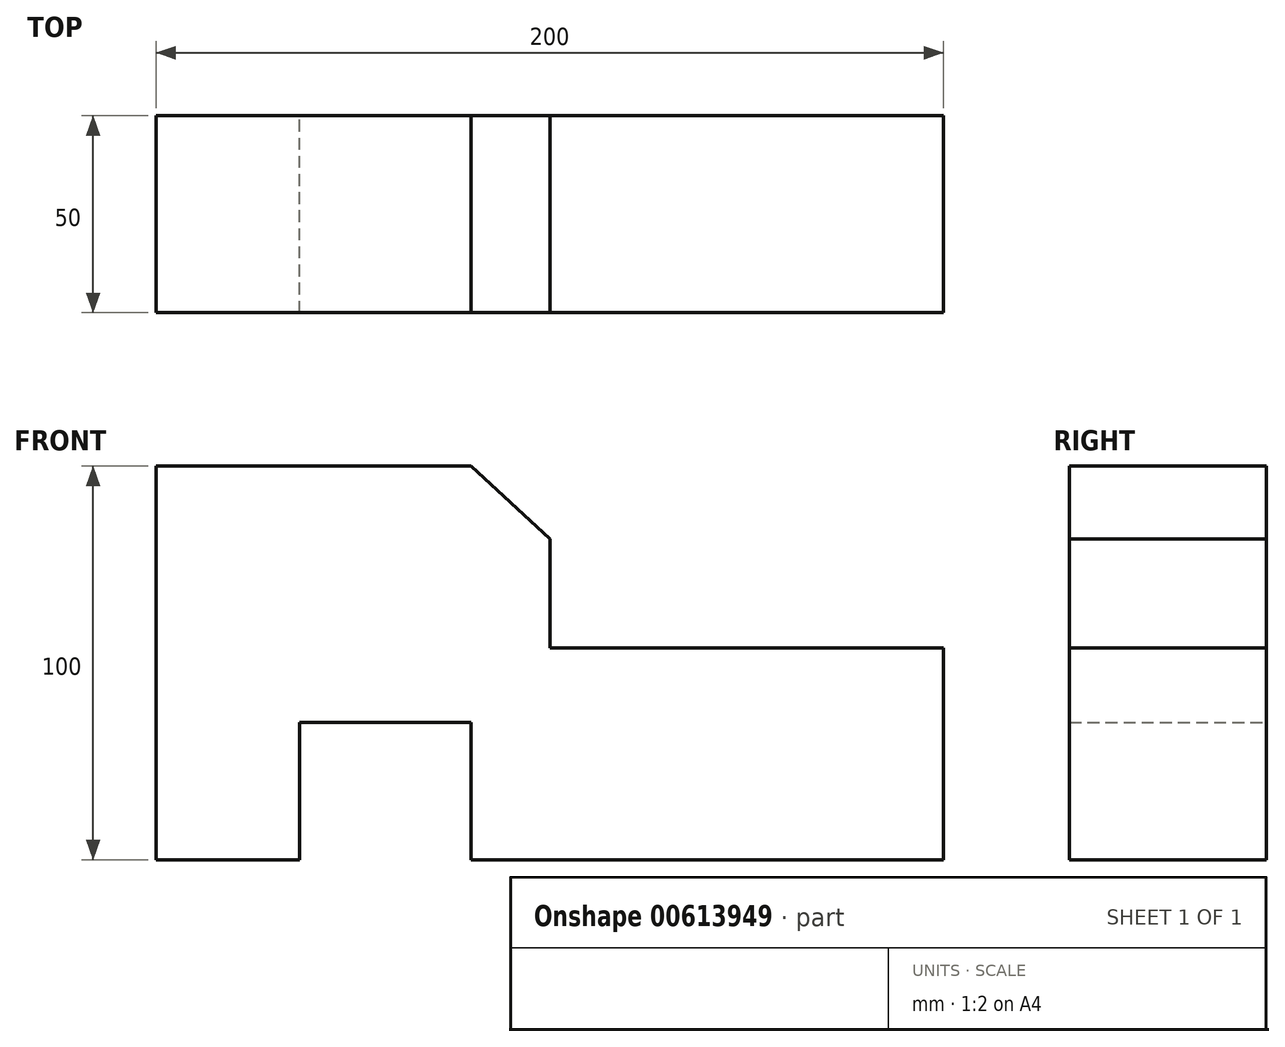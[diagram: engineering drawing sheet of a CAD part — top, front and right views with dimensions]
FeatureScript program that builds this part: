
annotation { "Feature Type Name" : "Feature", "Feature Type Description" : "" }
export const myFeature = defineFeature(function(context is Context, id is Id, definition is map)
    precondition{}
    {
        {
            var Q0;
            Q0=qCreatedBy(makeId("Front.planeOp"),FACE);
            var sketch = newSketch(context, id + "F0", { "sketchPlane" : qUnion([Q0])});
            skLineSegment(sketch, "E0", {"start": v(0, 0) * mm, "end": v(0, 100) * mm});
            skLineSegment(sketch, "E1", {"start": v(0, 100) * mm, "end": v(80, 100) * mm});
            skLineSegment(sketch, "E2", {"start": v(80, 100) * mm, "end": v(100, 81.45) * mm});
            skLineSegment(sketch, "E3", {"start": v(100, 81.45) * mm, "end": v(100, 53.85) * mm});
            skLineSegment(sketch, "E4", {"start": v(100, 53.85) * mm, "end": v(200, 53.85) * mm});
            skLineSegment(sketch, "E5", {"start": v(200, 53.85) * mm, "end": v(200, 0) * mm});
            skLineSegment(sketch, "E6", {"start": v(200, 0) * mm, "end": v(80, 0) * mm});
            skLineSegment(sketch, "E7", {"start": v(80, 0) * mm, "end": v(80, 34.84) * mm});
            skLineSegment(sketch, "E8", {"start": v(80, 34.84) * mm, "end": v(36.43, 34.84) * mm});
            skLineSegment(sketch, "E9", {"start": v(36.43, 34.84) * mm, "end": v(36.43, 0) * mm});
            skLineSegment(sketch, "E10", {"start": v(36.43, 0) * mm, "end": v(0, 0) * mm});
            skSolve(sketch);
        }
        {
            var Q0;
            Q0 = qSketchRegion(id + "F0", true);
            extrude(context, id + "F1", {"entities" : qUnion([Q0]), "depth" : 50 * mm, "offsetDistance" : 25 * mm});
        }
    });
